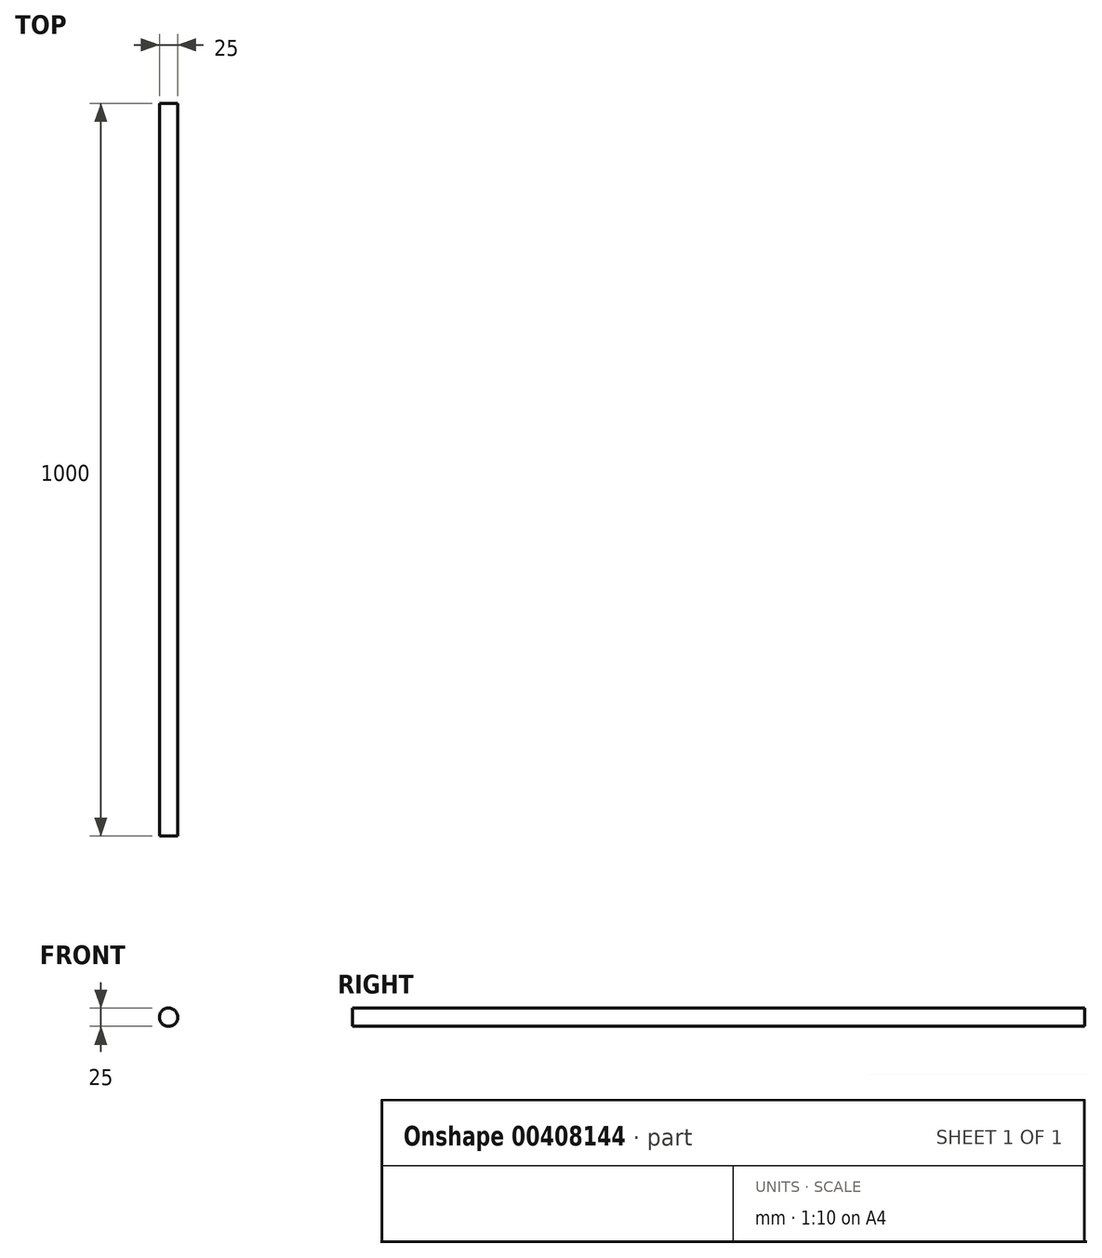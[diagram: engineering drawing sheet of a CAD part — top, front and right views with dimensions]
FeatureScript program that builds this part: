
annotation { "Feature Type Name" : "Feature", "Feature Type Description" : "" }
export const myFeature = defineFeature(function(context is Context, id is Id, definition is map)
    precondition{}
    {
        {
            var Q0;
            Q0=qCreatedBy(makeId("Front.planeOp"),FACE);
            var sketch = newSketch(context, id + "F0", { "sketchPlane" : qUnion([Q0])});
            skCircle(sketch, "E0", {"center": v(0, 0) * mm, "radius": 12.5 * mm});
            skSolve(sketch);
        }
        {
            var Q0;
            Q0=makeQuery(id+"F0.imprint","IMPRINT",FACE,{"disambiguationData":[TD([[makeQuery(id+"F0.imprint","IMPRINT",EDGE,{"derivedFrom":sQuery(id+"F0.wireOp",EDGE,"E0")}),1.0]])]});
            extrude(context, id + "F1", {"entities" : qUnion([Q0]), "endBound" : BoundingType.SYMMETRIC, "depth" : 1000 * mm});
        }
        {
            var Q0;
            Q0=qCreatedBy(makeId("Front.planeOp"),FACE);
            var sketch = newSketch(context, id + "F2", { "sketchPlane" : qUnion([Q0])});
            skLineSegment(sketch, "E1", {"start": v(-206.06, 0) * mm, "end": v(229.02, 0) * mm, "construction": true});
            skSolve(sketch);
        }
    });
